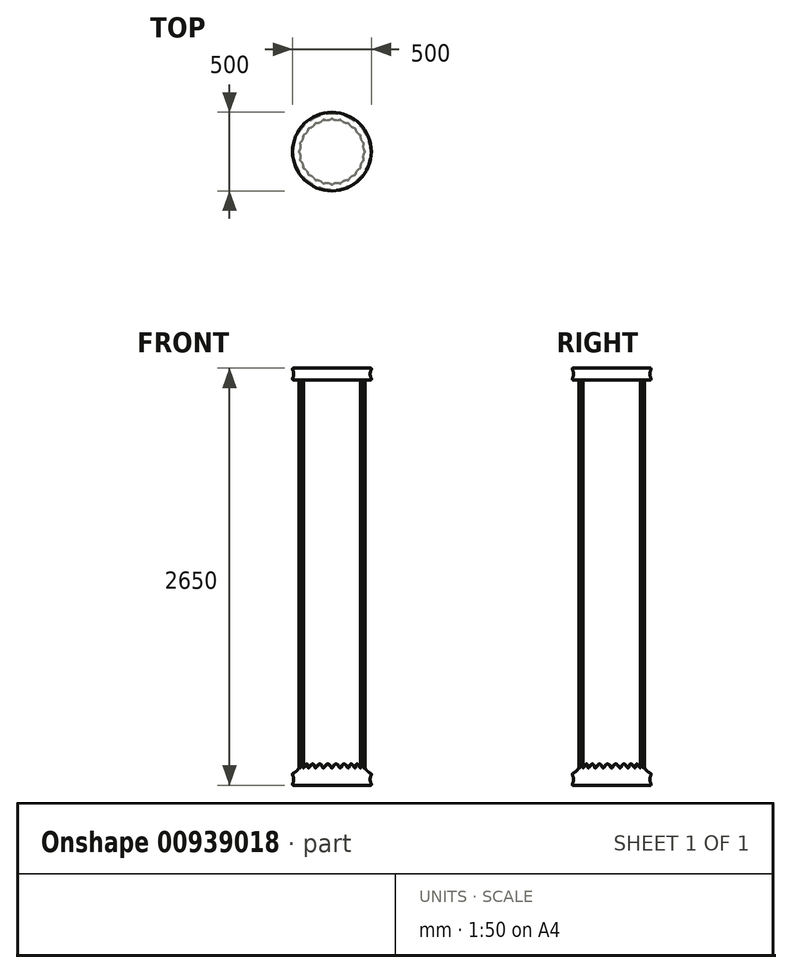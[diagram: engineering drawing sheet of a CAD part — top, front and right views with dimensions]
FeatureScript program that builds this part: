
annotation { "Feature Type Name" : "Feature", "Feature Type Description" : "" }
export const myFeature = defineFeature(function(context is Context, id is Id, definition is map)
    precondition{}
    {
        {
            var Q0;
            Q0=qCreatedBy(makeId("Front.planeOp"),FACE);
            var sketch = newSketch(context, id + "F0", { "sketchPlane" : qUnion([Q0])});
            skLineSegment(sketch, "E0", {"start": v(0, 0) * mm, "end": v(250, 0) * mm});
            skLineSegment(sketch, "E1", {"start": v(200, 147.6) * mm, "end": v(0, 147.6) * mm});
            skLineSegment(sketch, "E2", {"start": v(0, 147.6) * mm, "end": v(0, 0) * mm});
            skLineSegment(sketch, "E3", {"start": v(0, 147.6) * mm, "end": v(0, 2575) * mm});
            skLineSegment(sketch, "E4", {"start": v(0, 2575) * mm, "end": v(0, 2650) * mm});
            skLineSegment(sketch, "E5", {"start": v(0, 2650) * mm, "end": v(250, 2650) * mm});
            skLineSegment(sketch, "E6", {"start": v(250, 2575) * mm, "end": v(0, 2575) * mm});
            skLineSegment(sketch, "E7", {"start": v(250, 0) * mm, "end": v(250, 10) * mm});
            skArc(sketch, "E8", {"start": v(250, 65) * mm, "mid": v(242.63, 37.5) * mm, "end": v(250, 10) * mm});
            skLineSegment(sketch, "E9", {"start": v(250, 65) * mm, "end": v(250, 75) * mm});
            skLineSegment(sketch, "E10", {"start": v(250, 75) * mm, "end": v(200, 75) * mm});
            skLineSegment(sketch, "E11", {"start": v(200, 75) * mm, "end": v(200, 147.6) * mm});
            skLineSegment(sketch, "E12", {"start": v(250, 2650) * mm, "end": v(250, 2640) * mm});
            skLineSegment(sketch, "E13", {"start": v(250, 2575) * mm, "end": v(250, 2585) * mm});
            skArc(sketch, "E14", {"start": v(250, 2640) * mm, "mid": v(242.63, 2612.5) * mm, "end": v(250, 2585) * mm});
            skArc(sketch, "E15", {"start": v(200, 147.6) * mm, "mid": v(213.7, 103.52) * mm, "end": v(250, 75) * mm});
            skSolve(sketch);
        }
        {
            var Q0;
            Q0 = qSketchRegion(id + "F0", true);
            var Q1;
            Q1=sQuery(id+"F0.wireOp",EDGE,"E3");
            revolve(context, id + "F1", {"surfaceOperationType" : NewSurfaceOperationType.NEW, "entities" : qUnion([Q0]), "axis" : qUnion([Q1]), "revolveType" : RevolveType.FULL});
        }
        {
            var Q0;
            Q0=makeQuery(id+"F1.opRevolve","SWEPT_FACE",FACE,{"disambiguationData":[OSD([sQuery(id+"F0.wireOp",EDGE,"E1")])]});
            var sketch = newSketch(context, id + "F2", { "sketchPlane" : qUnion([Q0])});
            skCircle(sketch, "E16.cCircle", {"center": v(0, 0) * mm, "radius": 208.2 * mm, "construction": true});
            skLineSegment(sketch, "E16.0", {"start": v(202.84, 54.35) * mm, "end": v(210, 0) * mm});
            skLineSegment(sketch, "E16.1", {"start": v(210, 0) * mm, "end": v(202.84, -54.35) * mm});
            skLineSegment(sketch, "E16.2", {"start": v(202.84, -54.35) * mm, "end": v(181.87, -105) * mm});
            skLineSegment(sketch, "E16.3", {"start": v(181.87, -105) * mm, "end": v(148.5, -148.5) * mm});
            skLineSegment(sketch, "E16.4", {"start": v(148.5, -148.5) * mm, "end": v(105, -181.87) * mm});
            skLineSegment(sketch, "E16.5", {"start": v(105, -181.87) * mm, "end": v(54.35, -202.84) * mm});
            skLineSegment(sketch, "E16.6", {"start": v(54.35, -202.84) * mm, "end": v(0, -210) * mm});
            skLineSegment(sketch, "E16.7", {"start": v(0, -210) * mm, "end": v(-54.35, -202.84) * mm});
            skLineSegment(sketch, "E16.8", {"start": v(-54.35, -202.84) * mm, "end": v(-105, -181.87) * mm});
            skLineSegment(sketch, "E16.9", {"start": v(-105, -181.87) * mm, "end": v(-148.5, -148.5) * mm});
            skLineSegment(sketch, "E16.10", {"start": v(-148.5, -148.5) * mm, "end": v(-181.87, -105) * mm});
            skLineSegment(sketch, "E16.11", {"start": v(-181.87, -105) * mm, "end": v(-202.84, -54.35) * mm});
            skLineSegment(sketch, "E16.12", {"start": v(-202.84, -54.35) * mm, "end": v(-210, 0) * mm});
            skLineSegment(sketch, "E16.13", {"start": v(-210, 0) * mm, "end": v(-202.84, 54.35) * mm});
            skLineSegment(sketch, "E16.14", {"start": v(-202.84, 54.35) * mm, "end": v(-181.87, 105) * mm});
            skLineSegment(sketch, "E16.15", {"start": v(-181.87, 105) * mm, "end": v(-148.5, 148.5) * mm});
            skLineSegment(sketch, "E16.16", {"start": v(-148.5, 148.5) * mm, "end": v(-105, 181.87) * mm});
            skLineSegment(sketch, "E16.17", {"start": v(-105, 181.87) * mm, "end": v(-54.35, 202.84) * mm});
            skLineSegment(sketch, "E16.18", {"start": v(-54.35, 202.84) * mm, "end": v(0, 210) * mm});
            skLineSegment(sketch, "E16.19", {"start": v(0, 210) * mm, "end": v(54.35, 202.84) * mm});
            skLineSegment(sketch, "E16.20", {"start": v(54.35, 202.84) * mm, "end": v(105, 181.87) * mm});
            skLineSegment(sketch, "E16.21", {"start": v(105, 181.87) * mm, "end": v(148.5, 148.5) * mm});
            skLineSegment(sketch, "E16.22", {"start": v(148.5, 148.5) * mm, "end": v(181.87, 105) * mm});
            skLineSegment(sketch, "E16.23", {"start": v(181.87, 105) * mm, "end": v(202.84, 54.35) * mm});
            skLineSegment(sketch, "E17", {"start": v(0, 0) * mm, "end": v(210, 0) * mm});
            skArc(sketch, "E18", {"start": v(202.84, 54.35) * mm, "mid": v(199.17, 26.22) * mm, "end": v(210, 0) * mm});
            skArc(sketch, "E19", {"start": v(181.87, 105) * mm, "mid": v(185.6, 76.88) * mm, "end": v(202.84, 54.35) * mm});
            skArc(sketch, "E20", {"start": v(148.5, 148.5) * mm, "mid": v(159.37, 122.3) * mm, "end": v(181.87, 105) * mm});
            skArc(sketch, "E21", {"start": v(105, 181.87) * mm, "mid": v(122.3, 159.37) * mm, "end": v(148.5, 148.5) * mm});
            skArc(sketch, "E22", {"start": v(54.35, 202.84) * mm, "mid": v(76.88, 185.6) * mm, "end": v(105, 181.87) * mm});
            skArc(sketch, "E23", {"start": v(-54.35, 202.84) * mm, "mid": v(-26.22, 199.17) * mm, "end": v(0, 210) * mm});
            skArc(sketch, "E24", {"start": v(0, 210) * mm, "mid": v(26.22, 199.17) * mm, "end": v(54.35, 202.84) * mm});
            skArc(sketch, "E25", {"start": v(-105, 181.87) * mm, "mid": v(-76.88, 185.6) * mm, "end": v(-54.35, 202.84) * mm});
            skArc(sketch, "E26", {"start": v(-148.5, 148.5) * mm, "mid": v(-122.3, 159.37) * mm, "end": v(-105, 181.87) * mm});
            skArc(sketch, "E27", {"start": v(-181.87, 105) * mm, "mid": v(-159.37, 122.3) * mm, "end": v(-148.5, 148.5) * mm});
            skArc(sketch, "E28", {"start": v(-202.84, 54.35) * mm, "mid": v(-185.6, 76.88) * mm, "end": v(-181.87, 105) * mm});
            skArc(sketch, "E29", {"start": v(-210, 0) * mm, "mid": v(-199.17, 26.22) * mm, "end": v(-202.84, 54.35) * mm});
            skArc(sketch, "E30", {"start": v(-202.84, -54.35) * mm, "mid": v(-199.17, -26.22) * mm, "end": v(-210, 0) * mm});
            skArc(sketch, "E31", {"start": v(-181.87, -105) * mm, "mid": v(-185.6, -76.88) * mm, "end": v(-202.84, -54.35) * mm});
            skArc(sketch, "E32", {"start": v(-148.5, -148.5) * mm, "mid": v(-159.37, -122.3) * mm, "end": v(-181.87, -105) * mm});
            skArc(sketch, "E33", {"start": v(-105, -181.87) * mm, "mid": v(-122.3, -159.37) * mm, "end": v(-148.5, -148.5) * mm});
            skArc(sketch, "E34", {"start": v(-54.35, -202.84) * mm, "mid": v(-76.88, -185.6) * mm, "end": v(-105, -181.87) * mm});
            skArc(sketch, "E35", {"start": v(0, -210) * mm, "mid": v(-26.22, -199.17) * mm, "end": v(-54.35, -202.84) * mm});
            skArc(sketch, "E36", {"start": v(54.35, -202.84) * mm, "mid": v(26.22, -199.17) * mm, "end": v(0, -210) * mm});
            skArc(sketch, "E37", {"start": v(105, -181.87) * mm, "mid": v(76.88, -185.6) * mm, "end": v(54.35, -202.84) * mm});
            skArc(sketch, "E38", {"start": v(148.5, -148.5) * mm, "mid": v(122.3, -159.37) * mm, "end": v(105, -181.87) * mm});
            skArc(sketch, "E39", {"start": v(181.87, -105) * mm, "mid": v(159.37, -122.3) * mm, "end": v(148.5, -148.5) * mm});
            skArc(sketch, "E40", {"start": v(202.84, -54.35) * mm, "mid": v(185.6, -76.88) * mm, "end": v(181.87, -105) * mm});
            skArc(sketch, "E41", {"start": v(210, 0) * mm, "mid": v(199.17, -26.22) * mm, "end": v(202.84, -54.35) * mm});
            skSolve(sketch);
        }
        {
            var Q0;
            Q0=makeQuery(id+"F2.imprint","IMPRINT",FACE,{"disambiguationData":[TD([[makeQuery(id+"F2.imprint","IMPRINT",EDGE,{"derivedFrom":makeQuery(id+"F1.opRevolve","SWEPT_EDGE",EDGE,{"disambiguationData":[OSD([sQuery(id+"F0.wireOp",EDGE,"E1"),sQuery(id+"F0.wireOp",EDGE,"E11"),sQuery(id+"F0.wireOp",EDGE,"A7NMMrHn-6jUg-eE0d-P7Q7-RPc74vaHHU1M")])]})}),-1.0]])]});
            var Q1;
            Q1=makeQuery(id+"F2.imprint","IMPRINT",FACE,{"disambiguationData":[TD([[makeQuery(id+"F2.imprint","IMPRINT",EDGE,{"derivedFrom":sQuery(id+"F2.wireOp",EDGE,"E18")}),-1.0]])]});
            extrude(context, id + "F3", {"entities" : qUnion([Q0, Q1]), "operationType" : NewBodyOperationType.ADD, "depth" : 2500 * mm, "offsetDistance" : 25 * mm, "hasSecondDirection" : true, "secondDirectionOppositeDirection" : true, "secondDirectionDepth" : 50 * mm});
        }
        {
            var Q0;
            Q0=makeQuery(id+"F3.opExtrude","SWEPT_FACE",FACE,{"disambiguationData":[OSD([sQuery(id+"F2.wireOp",EDGE,"E35")])]});
            var Q1;
            Q1=makeQuery(id+"F1.opRevolve","SWEPT_FACE",FACE,{"disambiguationData":[OSD([sQuery(id+"F0.wireOp",EDGE,"E7")])]});
            var Q2;
            Q2=makeQuery(id+"F3.opExtrude","SWEPT_FACE",FACE,{"disambiguationData":[OSD([sQuery(id+"F2.wireOp",EDGE,"E36")])]});
            var Q3;
            Q3=makeQuery(id+"F3.opExtrude","SWEPT_FACE",FACE,{"disambiguationData":[OSD([sQuery(id+"F2.wireOp",EDGE,"E32")])]});
            var Q4;
            Q4=makeQuery(id+"F1.opRevolve","SWEPT_EDGE",EDGE,{"disambiguationData":[OSD([sQuery(id+"F0.wireOp",EDGE,"E0"),sQuery(id+"F0.wireOp",EDGE,"E7")])]});
            var Q5;
            Q5=makeQuery(id+"F1.opRevolve","SWEPT_EDGE",EDGE,{"disambiguationData":[OSD([sQuery(id+"F0.wireOp",EDGE,"E13"),sQuery(id+"F0.wireOp",EDGE,"E14")])]});
            var Q6;
            Q6=makeQuery(id+"F1.opRevolve","SWEPT_FACE",FACE,{"disambiguationData":[OSD([sQuery(id+"F0.wireOp",EDGE,"E13")])]});
            var Q7;
            Q7=makeQuery(id+"F1.opRevolve","SWEPT_FACE",FACE,{"disambiguationData":[OSD([sQuery(id+"F0.wireOp",EDGE,"E0")])]});
            var Q8;
            Q8=makeQuery(id+"F1.opRevolve","SWEPT_FACE",FACE,{"disambiguationData":[OSD([sQuery(id+"F0.wireOp",EDGE,"E12")])]});
            var Q9;
            Q9=makeQuery(id+"F1.opRevolve","SWEPT_FACE",FACE,{"disambiguationData":[OSD([sQuery(id+"F0.wireOp",EDGE,"E9")])]});
            var Q10;
            Q10=makeQuery(id+"F3.opExtrude","SWEPT_FACE",FACE,{"disambiguationData":[OSD([sQuery(id+"F2.wireOp",EDGE,"E38")])]});
            var Q11;
            Q11=makeQuery(id+"F1.opRevolve","SWEPT_FACE",FACE,{"disambiguationData":[OSD([sQuery(id+"F0.wireOp",EDGE,"E14")])]});
            var Q12;
            Q12=makeQuery(id+"F1.opRevolve","SWEPT_FACE",FACE,{"disambiguationData":[OSD([sQuery(id+"F0.wireOp",EDGE,"E6")])]});
            var Q13;
            Q13=makeQuery(id+"F3.opExtrude","SWEPT_FACE",FACE,{"disambiguationData":[OSD([sQuery(id+"F2.wireOp",EDGE,"E40")])]});
            var Q14;
            Q14=makeQuery(id+"F3.opExtrude","SWEPT_FACE",FACE,{"disambiguationData":[OSD([sQuery(id+"F2.wireOp",EDGE,"E33")])]});
            var Q15;
            Q15=makeQuery(id+"F1.opRevolve","SWEPT_FACE",FACE,{"disambiguationData":[OSD([sQuery(id+"F0.wireOp",EDGE,"E8")])]});
            var Q16;
            Q16=makeQuery(id+"F1.opRevolve","SWEPT_FACE",FACE,{"disambiguationData":[OSD([sQuery(id+"F0.wireOp",EDGE,"E15")])]});
            var Q17;
            Q17=makeQuery(id+"F3.opExtrude","SWEPT_FACE",FACE,{"disambiguationData":[OSD([sQuery(id+"F2.wireOp",EDGE,"E34")])]});
            var Q18;
            Q18=makeQuery(id+"F3.opExtrude","SWEPT_FACE",FACE,{"disambiguationData":[OSD([sQuery(id+"F2.wireOp",EDGE,"E37")])]});
            var Q19;
            Q19=makeQuery(id+"F1.opRevolve","SWEPT_EDGE",EDGE,{"disambiguationData":[OSD([sQuery(id+"F0.wireOp",EDGE,"E6"),sQuery(id+"F0.wireOp",EDGE,"E13")])]});
            var Q20;
            Q20=makeQuery(id+"F1.opRevolve","SWEPT_FACE",FACE,{"disambiguationData":[OSD([sQuery(id+"F0.wireOp",EDGE,"E5")])]});
            var Q21;
            Q21=makeQuery(id+"F3.opExtrude","SWEPT_FACE",FACE,{"disambiguationData":[OSD([sQuery(id+"F2.wireOp",EDGE,"E39")])]});
            var Q22;
            Q22=makeQuery(id+"F3.opExtrude","SWEPT_FACE",FACE,{"disambiguationData":[OSD([sQuery(id+"F2.wireOp",EDGE,"E31")])]});
            var Q23;
            Q23=makeQuery(id+"F3.boolean.opBoolean","INTERSECT",EDGE,{"derivedFrom":[makeQuery(id+"F1.opRevolve","SWEPT_FACE",FACE,{"disambiguationData":[OSD([sQuery(id+"F0.wireOp",EDGE,"E15")])]}),makeQuery(id+"F3.opExtrude","SWEPT_FACE",FACE,{"disambiguationData":[OSD([sQuery(id+"F2.wireOp",EDGE,"E39")])]})]});
            var Q24;
            Q24=makeQuery(id+"F3.opExtrude","SWEPT_FACE",FACE,{"disambiguationData":[OSD([sQuery(id+"F2.wireOp",EDGE,"E23")])]});
            var Q25;
            Q25=makeQuery(id+"F3.boolean.opBoolean","INTERSECT",EDGE,{"derivedFrom":[makeQuery(id+"F1.opRevolve","SWEPT_FACE",FACE,{"disambiguationData":[OSD([sQuery(id+"F0.wireOp",EDGE,"E15")])]}),makeQuery(id+"F3.opExtrude","SWEPT_FACE",FACE,{"disambiguationData":[OSD([sQuery(id+"F2.wireOp",EDGE,"E38")])]})]});
            var Q26;
            Q26=makeQuery(id+"F3.opExtrude","SWEPT_FACE",FACE,{"disambiguationData":[OSD([sQuery(id+"F2.wireOp",EDGE,"E20")])]});
            var Q27;
            Q27=makeQuery(id+"F3.boolean.opBoolean","INTERSECT",EDGE,{"derivedFrom":[makeQuery(id+"F1.opRevolve","SWEPT_FACE",FACE,{"disambiguationData":[OSD([sQuery(id+"F0.wireOp",EDGE,"E6")])]}),makeQuery(id+"F3.opExtrude","SWEPT_FACE",FACE,{"disambiguationData":[OSD([sQuery(id+"F2.wireOp",EDGE,"E38")])]})]});
            var Q28;
            Q28=makeQuery(id+"F3.opExtrude","SWEPT_EDGE",EDGE,{"disambiguationData":[OSD([sQuery(id+"F2.wireOp",EDGE,"E16.9"),sQuery(id+"F2.wireOp",EDGE,"E16.10"),sQuery(id+"F2.wireOp",EDGE,"E32"),sQuery(id+"F2.wireOp",EDGE,"E33")])]});
            var Q29;
            Q29=makeQuery(id+"F3.boolean.opBoolean","INTERSECT",EDGE,{"derivedFrom":[makeQuery(id+"F1.opRevolve","SWEPT_FACE",FACE,{"disambiguationData":[OSD([sQuery(id+"F0.wireOp",EDGE,"E6")])]}),makeQuery(id+"F3.opExtrude","SWEPT_FACE",FACE,{"disambiguationData":[OSD([sQuery(id+"F2.wireOp",EDGE,"E39")])]})]});
            var Q30;
            Q30=makeQuery(id+"F3.boolean.opBoolean","INTERSECT",EDGE,{"derivedFrom":[makeQuery(id+"F1.opRevolve","SWEPT_FACE",FACE,{"disambiguationData":[OSD([sQuery(id+"F0.wireOp",EDGE,"E6")])]}),makeQuery(id+"F3.opExtrude","SWEPT_FACE",FACE,{"disambiguationData":[OSD([sQuery(id+"F2.wireOp",EDGE,"E35")])]})]});
            var Q31;
            Q31=makeQuery(id+"F3.opExtrude","SWEPT_EDGE",EDGE,{"disambiguationData":[OSD([sQuery(id+"F2.wireOp",EDGE,"E16.3"),sQuery(id+"F2.wireOp",EDGE,"E16.4"),sQuery(id+"F2.wireOp",EDGE,"E38"),sQuery(id+"F2.wireOp",EDGE,"E39")])]});
            var Q32;
            Q32=makeQuery(id+"F3.boolean.opBoolean","INTERSECT",EDGE,{"derivedFrom":[makeQuery(id+"F1.opRevolve","SWEPT_FACE",FACE,{"disambiguationData":[OSD([sQuery(id+"F0.wireOp",EDGE,"E15")])]}),makeQuery(id+"F3.opExtrude","SWEPT_FACE",FACE,{"disambiguationData":[OSD([sQuery(id+"F2.wireOp",EDGE,"E35")])]})]});
            var Q33;
            Q33=makeQuery(id+"F3.boolean.opBoolean","INTERSECT",EDGE,{"derivedFrom":[makeQuery(id+"F1.opRevolve","SWEPT_FACE",FACE,{"disambiguationData":[OSD([sQuery(id+"F0.wireOp",EDGE,"E6")])]}),makeQuery(id+"F3.opExtrude","SWEPT_FACE",FACE,{"disambiguationData":[OSD([sQuery(id+"F2.wireOp",EDGE,"E36")])]})]});
            var Q34;
            Q34=makeQuery(id+"F3.boolean.opBoolean","INTERSECT",EDGE,{"derivedFrom":[makeQuery(id+"F1.opRevolve","SWEPT_FACE",FACE,{"disambiguationData":[OSD([sQuery(id+"F0.wireOp",EDGE,"E15")])]}),makeQuery(id+"F3.opExtrude","SWEPT_FACE",FACE,{"disambiguationData":[OSD([sQuery(id+"F2.wireOp",EDGE,"E31")])]})]});
            var Q35;
            Q35=makeQuery(id+"F3.opExtrude","SWEPT_FACE",FACE,{"disambiguationData":[OSD([sQuery(id+"F2.wireOp",EDGE,"E21")])]});
            var Q36;
            Q36=makeQuery(id+"F3.boolean.opBoolean","INTERSECT",EDGE,{"derivedFrom":[makeQuery(id+"F1.opRevolve","SWEPT_FACE",FACE,{"disambiguationData":[OSD([sQuery(id+"F0.wireOp",EDGE,"E15")])]}),makeQuery(id+"F3.opExtrude","SWEPT_FACE",FACE,{"disambiguationData":[OSD([sQuery(id+"F2.wireOp",EDGE,"E37")])]})]});
            var Q37;
            Q37=makeQuery(id+"F3.boolean.opBoolean","INTERSECT",EDGE,{"derivedFrom":[makeQuery(id+"F1.opRevolve","SWEPT_FACE",FACE,{"disambiguationData":[OSD([sQuery(id+"F0.wireOp",EDGE,"E15")])]}),makeQuery(id+"F3.opExtrude","SWEPT_FACE",FACE,{"disambiguationData":[OSD([sQuery(id+"F2.wireOp",EDGE,"E34")])]})]});
            var Q38;
            Q38=makeQuery(id+"F3.opExtrude","SWEPT_FACE",FACE,{"disambiguationData":[OSD([sQuery(id+"F2.wireOp",EDGE,"E22")])]});
            var Q39;
            Q39=makeQuery(id+"F3.opExtrude","SWEPT_EDGE",EDGE,{"disambiguationData":[OSD([sQuery(id+"F2.wireOp",EDGE,"E16.2"),sQuery(id+"F2.wireOp",EDGE,"E16.3"),sQuery(id+"F2.wireOp",EDGE,"E39"),sQuery(id+"F2.wireOp",EDGE,"E40")])]});
            var Q40;
            Q40=makeQuery(id+"F3.opExtrude","SWEPT_EDGE",EDGE,{"disambiguationData":[OSD([sQuery(id+"F2.wireOp",EDGE,"E16.6"),sQuery(id+"F2.wireOp",EDGE,"E16.7"),sQuery(id+"F2.wireOp",EDGE,"E35"),sQuery(id+"F2.wireOp",EDGE,"E36")])]});
            var Q41;
            Q41=makeQuery(id+"F3.opExtrude","SWEPT_EDGE",EDGE,{"disambiguationData":[OSD([sQuery(id+"F2.wireOp",EDGE,"E16.10"),sQuery(id+"F2.wireOp",EDGE,"E16.11"),sQuery(id+"F2.wireOp",EDGE,"E31"),sQuery(id+"F2.wireOp",EDGE,"E32")])]});
            var Q42;
            Q42=makeQuery(id+"F3.opExtrude","SWEPT_FACE",FACE,{"disambiguationData":[OSD([sQuery(id+"F2.wireOp",EDGE,"E27")])]});
            var Q43;
            Q43=makeQuery(id+"F3.opExtrude","SWEPT_FACE",FACE,{"disambiguationData":[OSD([sQuery(id+"F2.wireOp",EDGE,"E26")])]});
            var Q44;
            Q44=makeQuery(id+"F3.boolean.opBoolean","INTERSECT",EDGE,{"derivedFrom":[makeQuery(id+"F1.opRevolve","SWEPT_FACE",FACE,{"disambiguationData":[OSD([sQuery(id+"F0.wireOp",EDGE,"E6")])]}),makeQuery(id+"F3.opExtrude","SWEPT_FACE",FACE,{"disambiguationData":[OSD([sQuery(id+"F2.wireOp",EDGE,"E34")])]})]});
            var Q45;
            Q45=makeQuery(id+"F1.opRevolve","SWEPT_EDGE",EDGE,{"disambiguationData":[OSD([sQuery(id+"F0.wireOp",EDGE,"E7"),sQuery(id+"F0.wireOp",EDGE,"E8")])]});
            var Q46;
            Q46=makeQuery(id+"F3.boolean.opBoolean","INTERSECT",EDGE,{"derivedFrom":[makeQuery(id+"F1.opRevolve","SWEPT_FACE",FACE,{"disambiguationData":[OSD([sQuery(id+"F0.wireOp",EDGE,"E15")])]}),makeQuery(id+"F3.opExtrude","SWEPT_FACE",FACE,{"disambiguationData":[OSD([sQuery(id+"F2.wireOp",EDGE,"E32")])]})]});
            var Q47;
            Q47=makeQuery(id+"F3.opExtrude","SWEPT_EDGE",EDGE,{"disambiguationData":[OSD([sQuery(id+"F2.wireOp",EDGE,"E16.5"),sQuery(id+"F2.wireOp",EDGE,"E16.6"),sQuery(id+"F2.wireOp",EDGE,"E36"),sQuery(id+"F2.wireOp",EDGE,"E37")])]});
            var Q48;
            Q48=makeQuery(id+"F3.opExtrude","SWEPT_FACE",FACE,{"disambiguationData":[OSD([sQuery(id+"F2.wireOp",EDGE,"E41")])]});
            var Q49;
            Q49=makeQuery(id+"F3.boolean.opBoolean","INTERSECT",EDGE,{"derivedFrom":[makeQuery(id+"F1.opRevolve","SWEPT_FACE",FACE,{"disambiguationData":[OSD([sQuery(id+"F0.wireOp",EDGE,"E6")])]}),makeQuery(id+"F3.opExtrude","SWEPT_FACE",FACE,{"disambiguationData":[OSD([sQuery(id+"F2.wireOp",EDGE,"E37")])]})]});
            var Q50;
            Q50=makeQuery(id+"F3.opExtrude","SWEPT_FACE",FACE,{"disambiguationData":[OSD([sQuery(id+"F2.wireOp",EDGE,"E25")])]});
            var Q51;
            Q51=makeQuery(id+"F3.boolean.opBoolean","INTERSECT",EDGE,{"derivedFrom":[makeQuery(id+"F1.opRevolve","SWEPT_FACE",FACE,{"disambiguationData":[OSD([sQuery(id+"F0.wireOp",EDGE,"E15")])]}),makeQuery(id+"F3.opExtrude","SWEPT_FACE",FACE,{"disambiguationData":[OSD([sQuery(id+"F2.wireOp",EDGE,"E33")])]})]});
            var Q52;
            Q52=makeQuery(id+"F3.opExtrude","SWEPT_EDGE",EDGE,{"disambiguationData":[OSD([sQuery(id+"F2.wireOp",EDGE,"E16.8"),sQuery(id+"F2.wireOp",EDGE,"E16.9"),sQuery(id+"F2.wireOp",EDGE,"E33"),sQuery(id+"F2.wireOp",EDGE,"E34")])]});
            var Q53;
            Q53=makeQuery(id+"F3.boolean.opBoolean","INTERSECT",EDGE,{"derivedFrom":[makeQuery(id+"F1.opRevolve","SWEPT_FACE",FACE,{"disambiguationData":[OSD([sQuery(id+"F0.wireOp",EDGE,"E15")])]}),makeQuery(id+"F3.opExtrude","SWEPT_FACE",FACE,{"disambiguationData":[OSD([sQuery(id+"F2.wireOp",EDGE,"E36")])]})]});
            var Q54;
            Q54=makeQuery(id+"F3.opExtrude","SWEPT_FACE",FACE,{"disambiguationData":[OSD([sQuery(id+"F2.wireOp",EDGE,"E30")])]});
            var Q55;
            Q55=makeQuery(id+"F3.opExtrude","SWEPT_EDGE",EDGE,{"disambiguationData":[OSD([sQuery(id+"F2.wireOp",EDGE,"E16.7"),sQuery(id+"F2.wireOp",EDGE,"E16.8"),sQuery(id+"F2.wireOp",EDGE,"E34"),sQuery(id+"F2.wireOp",EDGE,"E35")])]});
            var Q56;
            Q56=makeQuery(id+"F1.opRevolve","SWEPT_EDGE",EDGE,{"disambiguationData":[OSD([sQuery(id+"F0.wireOp",EDGE,"E12"),sQuery(id+"F0.wireOp",EDGE,"E14")])]});
            var Q57;
            Q57=makeQuery(id+"F3.opExtrude","SWEPT_EDGE",EDGE,{"disambiguationData":[OSD([sQuery(id+"F2.wireOp",EDGE,"E16.4"),sQuery(id+"F2.wireOp",EDGE,"E16.5"),sQuery(id+"F2.wireOp",EDGE,"E37"),sQuery(id+"F2.wireOp",EDGE,"E38")])]});
            var Q58;
            Q58=makeQuery(id+"F3.boolean.opBoolean","INTERSECT",EDGE,{"derivedFrom":[makeQuery(id+"F1.opRevolve","SWEPT_FACE",FACE,{"disambiguationData":[OSD([sQuery(id+"F0.wireOp",EDGE,"E6")])]}),makeQuery(id+"F3.opExtrude","SWEPT_FACE",FACE,{"disambiguationData":[OSD([sQuery(id+"F2.wireOp",EDGE,"E33")])]})]});
            var Q59;
            Q59=makeQuery(id+"F3.boolean.opBoolean","INTERSECT",EDGE,{"derivedFrom":[makeQuery(id+"F1.opRevolve","SWEPT_FACE",FACE,{"disambiguationData":[OSD([sQuery(id+"F0.wireOp",EDGE,"E6")])]}),makeQuery(id+"F3.opExtrude","SWEPT_FACE",FACE,{"disambiguationData":[OSD([sQuery(id+"F2.wireOp",EDGE,"E32")])]})]});
            var Q60;
            Q60=makeQuery(id+"F3.boolean.opBoolean","INTERSECT",EDGE,{"derivedFrom":[makeQuery(id+"F1.opRevolve","SWEPT_FACE",FACE,{"disambiguationData":[OSD([sQuery(id+"F0.wireOp",EDGE,"E6")])]}),makeQuery(id+"F3.opExtrude","SWEPT_FACE",FACE,{"disambiguationData":[OSD([sQuery(id+"F2.wireOp",EDGE,"E31")])]})]});
            var Q61;
            Q61=makeQuery(id+"F3.boolean.opBoolean","INTERSECT",EDGE,{"derivedFrom":[makeQuery(id+"F1.opRevolve","SWEPT_FACE",FACE,{"disambiguationData":[OSD([sQuery(id+"F0.wireOp",EDGE,"E6")])]}),makeQuery(id+"F3.opExtrude","SWEPT_FACE",FACE,{"disambiguationData":[OSD([sQuery(id+"F2.wireOp",EDGE,"E40")])]})]});
            var Q62;
            Q62=makeQuery(id+"F1.opRevolve","SWEPT_EDGE",EDGE,{"disambiguationData":[OSD([sQuery(id+"F0.wireOp",EDGE,"E9"),sQuery(id+"F0.wireOp",EDGE,"E10"),sQuery(id+"F0.wireOp",EDGE,"E15")])]});
            var Q63;
            Q63=makeQuery(id+"F3.boolean.opBoolean","INTERSECT",EDGE,{"derivedFrom":[makeQuery(id+"F1.opRevolve","SWEPT_FACE",FACE,{"disambiguationData":[OSD([sQuery(id+"F0.wireOp",EDGE,"E15")])]}),makeQuery(id+"F3.opExtrude","SWEPT_FACE",FACE,{"disambiguationData":[OSD([sQuery(id+"F2.wireOp",EDGE,"E40")])]})]});
            var Q64;
            Q64=makeQuery(id+"F3.opExtrude","SWEPT_FACE",FACE,{"disambiguationData":[OSD([sQuery(id+"F2.wireOp",EDGE,"E24")])]});
            var Q65;
            Q65=makeQuery(id+"F3.opExtrude","SWEPT_EDGE",EDGE,{"disambiguationData":[OSD([sQuery(id+"F2.wireOp",EDGE,"E16.1"),sQuery(id+"F2.wireOp",EDGE,"E16.2"),sQuery(id+"F2.wireOp",EDGE,"E40"),sQuery(id+"F2.wireOp",EDGE,"E41")])]});
            var Q66;
            Q66=makeQuery(id+"F3.boolean.opBoolean","INTERSECT",EDGE,{"derivedFrom":[makeQuery(id+"F1.opRevolve","SWEPT_FACE",FACE,{"disambiguationData":[OSD([sQuery(id+"F0.wireOp",EDGE,"E15")])]}),makeQuery(id+"F3.opExtrude","SWEPT_FACE",FACE,{"disambiguationData":[OSD([sQuery(id+"F2.wireOp",EDGE,"E30")])]})]});
            var Q67;
            Q67=makeQuery(id+"F3.opExtrude","SWEPT_EDGE",EDGE,{"disambiguationData":[OSD([sQuery(id+"F2.wireOp",EDGE,"E16.21"),sQuery(id+"F2.wireOp",EDGE,"E16.22"),sQuery(id+"F2.wireOp",EDGE,"E20"),sQuery(id+"F2.wireOp",EDGE,"E21")])]});
            var Q68;
            Q68=makeQuery(id+"F3.boolean.opBoolean","INTERSECT",EDGE,{"derivedFrom":[makeQuery(id+"F1.opRevolve","SWEPT_FACE",FACE,{"disambiguationData":[OSD([sQuery(id+"F0.wireOp",EDGE,"E6")])]}),makeQuery(id+"F3.opExtrude","SWEPT_FACE",FACE,{"disambiguationData":[OSD([sQuery(id+"F2.wireOp",EDGE,"E27")])]})]});
            var Q69;
            Q69=makeQuery(id+"F3.opExtrude","SWEPT_FACE",FACE,{"disambiguationData":[OSD([sQuery(id+"F2.wireOp",EDGE,"E28")])]});
            var Q70;
            Q70=makeQuery(id+"F3.opExtrude","SWEPT_FACE",FACE,{"disambiguationData":[OSD([sQuery(id+"F2.wireOp",EDGE,"E18")])]});
            var Q71;
            Q71=makeQuery(id+"F3.boolean.opBoolean","INTERSECT",EDGE,{"derivedFrom":[makeQuery(id+"F1.opRevolve","SWEPT_FACE",FACE,{"disambiguationData":[OSD([sQuery(id+"F0.wireOp",EDGE,"E15")])]}),makeQuery(id+"F3.opExtrude","SWEPT_FACE",FACE,{"disambiguationData":[OSD([sQuery(id+"F2.wireOp",EDGE,"E25")])]})]});
            var Q72;
            Q72=makeQuery(id+"F3.boolean.opBoolean","INTERSECT",EDGE,{"derivedFrom":[makeQuery(id+"F1.opRevolve","SWEPT_FACE",FACE,{"disambiguationData":[OSD([sQuery(id+"F0.wireOp",EDGE,"E15")])]}),makeQuery(id+"F3.opExtrude","SWEPT_FACE",FACE,{"disambiguationData":[OSD([sQuery(id+"F2.wireOp",EDGE,"E20")])]})]});
            var Q73;
            Q73=makeQuery(id+"F3.boolean.opBoolean","INTERSECT",EDGE,{"derivedFrom":[makeQuery(id+"F1.opRevolve","SWEPT_FACE",FACE,{"disambiguationData":[OSD([sQuery(id+"F0.wireOp",EDGE,"E6")])]}),makeQuery(id+"F3.opExtrude","SWEPT_FACE",FACE,{"disambiguationData":[OSD([sQuery(id+"F2.wireOp",EDGE,"E20")])]})]});
            var Q74;
            Q74=makeQuery(id+"F3.opExtrude","SWEPT_FACE",FACE,{"disambiguationData":[OSD([sQuery(id+"F2.wireOp",EDGE,"E19")])]});
            var Q75;
            Q75=makeQuery(id+"F3.boolean.opBoolean","INTERSECT",EDGE,{"derivedFrom":[makeQuery(id+"F1.opRevolve","SWEPT_FACE",FACE,{"disambiguationData":[OSD([sQuery(id+"F0.wireOp",EDGE,"E15")])]}),makeQuery(id+"F3.opExtrude","SWEPT_FACE",FACE,{"disambiguationData":[OSD([sQuery(id+"F2.wireOp",EDGE,"E28")])]})]});
            var Q76;
            Q76=makeQuery(id+"F3.boolean.opBoolean","INTERSECT",EDGE,{"derivedFrom":[makeQuery(id+"F1.opRevolve","SWEPT_FACE",FACE,{"disambiguationData":[OSD([sQuery(id+"F0.wireOp",EDGE,"E15")])]}),makeQuery(id+"F3.opExtrude","SWEPT_FACE",FACE,{"disambiguationData":[OSD([sQuery(id+"F2.wireOp",EDGE,"E22")])]})]});
            var Q77;
            Q77=makeQuery(id+"F3.opExtrude","SWEPT_EDGE",EDGE,{"disambiguationData":[OSD([sQuery(id+"F2.wireOp",EDGE,"E16.15"),sQuery(id+"F2.wireOp",EDGE,"E16.16"),sQuery(id+"F2.wireOp",EDGE,"E26"),sQuery(id+"F2.wireOp",EDGE,"E27")])]});
            var Q78;
            Q78=makeQuery(id+"F3.opExtrude","SWEPT_FACE",FACE,{"disambiguationData":[OSD([sQuery(id+"F2.wireOp",EDGE,"E29")])]});
            var Q79;
            Q79=makeQuery(id+"F3.opExtrude","SWEPT_EDGE",EDGE,{"disambiguationData":[OSD([sQuery(id+"F2.wireOp",EDGE,"E16.11"),sQuery(id+"F2.wireOp",EDGE,"E16.12"),sQuery(id+"F2.wireOp",EDGE,"E30"),sQuery(id+"F2.wireOp",EDGE,"E31")])]});
            var Q80;
            Q80=makeQuery(id+"F1.opRevolve","SWEPT_EDGE",EDGE,{"disambiguationData":[OSD([sQuery(id+"F0.wireOp",EDGE,"E5"),sQuery(id+"F0.wireOp",EDGE,"E12")])]});
            var Q81;
            Q81=makeQuery(id+"F3.boolean.opBoolean","INTERSECT",EDGE,{"derivedFrom":[makeQuery(id+"F1.opRevolve","SWEPT_FACE",FACE,{"disambiguationData":[OSD([sQuery(id+"F0.wireOp",EDGE,"E15")])]}),makeQuery(id+"F3.opExtrude","SWEPT_FACE",FACE,{"disambiguationData":[OSD([sQuery(id+"F2.wireOp",EDGE,"E19")])]})]});
            var Q82;
            Q82=makeQuery(id+"F3.boolean.opBoolean","INTERSECT",EDGE,{"derivedFrom":[makeQuery(id+"F1.opRevolve","SWEPT_FACE",FACE,{"disambiguationData":[OSD([sQuery(id+"F0.wireOp",EDGE,"E6")])]}),makeQuery(id+"F3.opExtrude","SWEPT_FACE",FACE,{"disambiguationData":[OSD([sQuery(id+"F2.wireOp",EDGE,"E22")])]})]});
            var Q83;
            Q83=makeQuery(id+"F3.boolean.opBoolean","INTERSECT",EDGE,{"derivedFrom":[makeQuery(id+"F1.opRevolve","SWEPT_FACE",FACE,{"disambiguationData":[OSD([sQuery(id+"F0.wireOp",EDGE,"E15")])]}),makeQuery(id+"F3.opExtrude","SWEPT_FACE",FACE,{"disambiguationData":[OSD([sQuery(id+"F2.wireOp",EDGE,"E21")])]})]});
            var Q84;
            Q84=makeQuery(id+"F3.boolean.opBoolean","INTERSECT",EDGE,{"derivedFrom":[makeQuery(id+"F1.opRevolve","SWEPT_FACE",FACE,{"disambiguationData":[OSD([sQuery(id+"F0.wireOp",EDGE,"E6")])]}),makeQuery(id+"F3.opExtrude","SWEPT_FACE",FACE,{"disambiguationData":[OSD([sQuery(id+"F2.wireOp",EDGE,"E30")])]})]});
            var Q85;
            Q85=makeQuery(id+"F3.boolean.opBoolean","INTERSECT",EDGE,{"derivedFrom":[makeQuery(id+"F1.opRevolve","SWEPT_FACE",FACE,{"disambiguationData":[OSD([sQuery(id+"F0.wireOp",EDGE,"E6")])]}),makeQuery(id+"F3.opExtrude","SWEPT_FACE",FACE,{"disambiguationData":[OSD([sQuery(id+"F2.wireOp",EDGE,"E23")])]})]});
            var Q86;
            Q86=makeQuery(id+"F3.boolean.opBoolean","INTERSECT",EDGE,{"derivedFrom":[makeQuery(id+"F1.opRevolve","SWEPT_FACE",FACE,{"disambiguationData":[OSD([sQuery(id+"F0.wireOp",EDGE,"E6")])]}),makeQuery(id+"F3.opExtrude","SWEPT_FACE",FACE,{"disambiguationData":[OSD([sQuery(id+"F2.wireOp",EDGE,"E24")])]})]});
            var Q87;
            Q87=makeQuery(id+"F3.boolean.opBoolean","INTERSECT",EDGE,{"derivedFrom":[makeQuery(id+"F1.opRevolve","SWEPT_FACE",FACE,{"disambiguationData":[OSD([sQuery(id+"F0.wireOp",EDGE,"E6")])]}),makeQuery(id+"F3.opExtrude","SWEPT_FACE",FACE,{"disambiguationData":[OSD([sQuery(id+"F2.wireOp",EDGE,"E21")])]})]});
            var Q88;
            Q88=makeQuery(id+"F3.opExtrude","SWEPT_EDGE",EDGE,{"disambiguationData":[OSD([sQuery(id+"F2.wireOp",EDGE,"E16.17"),sQuery(id+"F2.wireOp",EDGE,"E16.18"),sQuery(id+"F2.wireOp",EDGE,"E23"),sQuery(id+"F2.wireOp",EDGE,"E25")])]});
            var Q89;
            Q89=makeQuery(id+"F3.boolean.opBoolean","INTERSECT",EDGE,{"derivedFrom":[makeQuery(id+"F1.opRevolve","SWEPT_FACE",FACE,{"disambiguationData":[OSD([sQuery(id+"F0.wireOp",EDGE,"E15")])]}),makeQuery(id+"F3.opExtrude","SWEPT_FACE",FACE,{"disambiguationData":[OSD([sQuery(id+"F2.wireOp",EDGE,"E26")])]})]});
            var Q90;
            Q90=makeQuery(id+"F3.opExtrude","SWEPT_EDGE",EDGE,{"disambiguationData":[OSD([sQuery(id+"F2.wireOp",EDGE,"E16.20"),sQuery(id+"F2.wireOp",EDGE,"E16.21"),sQuery(id+"F2.wireOp",EDGE,"E21"),sQuery(id+"F2.wireOp",EDGE,"E22")])]});
            var Q91;
            Q91=makeQuery(id+"F3.opExtrude","SWEPT_EDGE",EDGE,{"disambiguationData":[OSD([sQuery(id+"F2.wireOp",EDGE,"E16.16"),sQuery(id+"F2.wireOp",EDGE,"E16.17"),sQuery(id+"F2.wireOp",EDGE,"E25"),sQuery(id+"F2.wireOp",EDGE,"E26")])]});
            var Q92;
            Q92=makeQuery(id+"F3.boolean.opBoolean","INTERSECT",EDGE,{"derivedFrom":[makeQuery(id+"F1.opRevolve","SWEPT_FACE",FACE,{"disambiguationData":[OSD([sQuery(id+"F0.wireOp",EDGE,"E6")])]}),makeQuery(id+"F3.opExtrude","SWEPT_FACE",FACE,{"disambiguationData":[OSD([sQuery(id+"F2.wireOp",EDGE,"E26")])]})]});
            var Q93;
            Q93=makeQuery(id+"F3.boolean.opBoolean","INTERSECT",EDGE,{"derivedFrom":[makeQuery(id+"F1.opRevolve","SWEPT_FACE",FACE,{"disambiguationData":[OSD([sQuery(id+"F0.wireOp",EDGE,"E6")])]}),makeQuery(id+"F3.opExtrude","SWEPT_FACE",FACE,{"disambiguationData":[OSD([sQuery(id+"F2.wireOp",EDGE,"E41")])]})]});
            var Q94;
            Q94=makeQuery(id+"F3.boolean.opBoolean","INTERSECT",EDGE,{"derivedFrom":[makeQuery(id+"F1.opRevolve","SWEPT_FACE",FACE,{"disambiguationData":[OSD([sQuery(id+"F0.wireOp",EDGE,"E6")])]}),makeQuery(id+"F3.opExtrude","SWEPT_FACE",FACE,{"disambiguationData":[OSD([sQuery(id+"F2.wireOp",EDGE,"E25")])]})]});
            var Q95;
            Q95=makeQuery(id+"F3.boolean.opBoolean","INTERSECT",EDGE,{"derivedFrom":[makeQuery(id+"F1.opRevolve","SWEPT_FACE",FACE,{"disambiguationData":[OSD([sQuery(id+"F0.wireOp",EDGE,"E15")])]}),makeQuery(id+"F3.opExtrude","SWEPT_FACE",FACE,{"disambiguationData":[OSD([sQuery(id+"F2.wireOp",EDGE,"E24")])]})]});
            var Q96;
            Q96=makeQuery(id+"F3.boolean.opBoolean","INTERSECT",EDGE,{"derivedFrom":[makeQuery(id+"F1.opRevolve","SWEPT_FACE",FACE,{"disambiguationData":[OSD([sQuery(id+"F0.wireOp",EDGE,"E15")])]}),makeQuery(id+"F3.opExtrude","SWEPT_FACE",FACE,{"disambiguationData":[OSD([sQuery(id+"F2.wireOp",EDGE,"E23")])]})]});
            var Q97;
            Q97=makeQuery(id+"F3.boolean.opBoolean","INTERSECT",EDGE,{"derivedFrom":[makeQuery(id+"F1.opRevolve","SWEPT_FACE",FACE,{"disambiguationData":[OSD([sQuery(id+"F0.wireOp",EDGE,"E15")])]}),makeQuery(id+"F3.opExtrude","SWEPT_FACE",FACE,{"disambiguationData":[OSD([sQuery(id+"F2.wireOp",EDGE,"E27")])]})]});
            var Q98;
            Q98=makeQuery(id+"F3.opExtrude","SWEPT_EDGE",EDGE,{"disambiguationData":[OSD([sQuery(id+"F2.wireOp",EDGE,"E16.19"),sQuery(id+"F2.wireOp",EDGE,"E16.20"),sQuery(id+"F2.wireOp",EDGE,"E22"),sQuery(id+"F2.wireOp",EDGE,"E24")])]});
            var Q99;
            Q99=makeQuery(id+"F1.opRevolve","SWEPT_EDGE",EDGE,{"disambiguationData":[OSD([sQuery(id+"F0.wireOp",EDGE,"E8"),sQuery(id+"F0.wireOp",EDGE,"E9")])]});
            var Q100;
            Q100=makeQuery(id+"F3.opExtrude","SWEPT_EDGE",EDGE,{"disambiguationData":[OSD([sQuery(id+"F2.wireOp",EDGE,"E16.18"),sQuery(id+"F2.wireOp",EDGE,"E16.19"),sQuery(id+"F2.wireOp",EDGE,"E23"),sQuery(id+"F2.wireOp",EDGE,"E24")])]});
            var Q101;
            Q101=makeQuery(id+"F3.boolean.opBoolean","INTERSECT",EDGE,{"derivedFrom":[makeQuery(id+"F1.opRevolve","SWEPT_FACE",FACE,{"disambiguationData":[OSD([sQuery(id+"F0.wireOp",EDGE,"E15")])]}),makeQuery(id+"F3.opExtrude","SWEPT_FACE",FACE,{"disambiguationData":[OSD([sQuery(id+"F2.wireOp",EDGE,"E41")])]})]});
            var Q102;
            Q102=makeQuery(id+"F3.boolean.opBoolean","INTERSECT",EDGE,{"derivedFrom":[makeQuery(id+"F1.opRevolve","SWEPT_FACE",FACE,{"disambiguationData":[OSD([sQuery(id+"F0.wireOp",EDGE,"E6")])]}),makeQuery(id+"F3.opExtrude","SWEPT_FACE",FACE,{"disambiguationData":[OSD([sQuery(id+"F2.wireOp",EDGE,"E28")])]})]});
            var Q103;
            Q103=makeQuery(id+"F3.opExtrude","SWEPT_EDGE",EDGE,{"disambiguationData":[OSD([sQuery(id+"F2.wireOp",EDGE,"E16.22"),sQuery(id+"F2.wireOp",EDGE,"E16.23"),sQuery(id+"F2.wireOp",EDGE,"E19"),sQuery(id+"F2.wireOp",EDGE,"E20")])]});
            var Q104;
            Q104=makeQuery(id+"F3.boolean.opBoolean","INTERSECT",EDGE,{"derivedFrom":[makeQuery(id+"F1.opRevolve","SWEPT_FACE",FACE,{"disambiguationData":[OSD([sQuery(id+"F0.wireOp",EDGE,"E6")])]}),makeQuery(id+"F3.opExtrude","SWEPT_FACE",FACE,{"disambiguationData":[OSD([sQuery(id+"F2.wireOp",EDGE,"E19")])]})]});
            var Q105;
            Q105=makeQuery(id+"F3.opExtrude","SWEPT_EDGE",EDGE,{"disambiguationData":[OSD([sQuery(id+"F2.wireOp",EDGE,"E16.0"),sQuery(id+"F2.wireOp",EDGE,"E16.1"),sQuery(id+"F2.wireOp",EDGE,"E18"),sQuery(id+"F2.wireOp",EDGE,"E41")])]});
            var Q106;
            Q106=makeQuery(id+"F3.boolean.opBoolean","INTERSECT",EDGE,{"derivedFrom":[makeQuery(id+"F1.opRevolve","SWEPT_FACE",FACE,{"disambiguationData":[OSD([sQuery(id+"F0.wireOp",EDGE,"E6")])]}),makeQuery(id+"F3.opExtrude","SWEPT_FACE",FACE,{"disambiguationData":[OSD([sQuery(id+"F2.wireOp",EDGE,"E18")])]})]});
            var Q107;
            Q107=makeQuery(id+"F3.opExtrude","SWEPT_EDGE",EDGE,{"disambiguationData":[OSD([sQuery(id+"F2.wireOp",EDGE,"E16.12"),sQuery(id+"F2.wireOp",EDGE,"E16.13"),sQuery(id+"F2.wireOp",EDGE,"E29"),sQuery(id+"F2.wireOp",EDGE,"E30")])]});
            var Q108;
            Q108=makeQuery(id+"F3.boolean.opBoolean","INTERSECT",EDGE,{"derivedFrom":[makeQuery(id+"F1.opRevolve","SWEPT_FACE",FACE,{"disambiguationData":[OSD([sQuery(id+"F0.wireOp",EDGE,"E15")])]}),makeQuery(id+"F3.opExtrude","SWEPT_FACE",FACE,{"disambiguationData":[OSD([sQuery(id+"F2.wireOp",EDGE,"E29")])]})]});
            var Q109;
            Q109=makeQuery(id+"F3.boolean.opBoolean","INTERSECT",EDGE,{"derivedFrom":[makeQuery(id+"F1.opRevolve","SWEPT_FACE",FACE,{"disambiguationData":[OSD([sQuery(id+"F0.wireOp",EDGE,"E6")])]}),makeQuery(id+"F3.opExtrude","SWEPT_FACE",FACE,{"disambiguationData":[OSD([sQuery(id+"F2.wireOp",EDGE,"E29")])]})]});
            var Q110;
            Q110=makeQuery(id+"F3.boolean.opBoolean","INTERSECT",EDGE,{"derivedFrom":[makeQuery(id+"F1.opRevolve","SWEPT_FACE",FACE,{"disambiguationData":[OSD([sQuery(id+"F0.wireOp",EDGE,"E15")])]}),makeQuery(id+"F3.opExtrude","SWEPT_FACE",FACE,{"disambiguationData":[OSD([sQuery(id+"F2.wireOp",EDGE,"E18")])]})]});
            var Q111;
            Q111=makeQuery(id+"F3.opExtrude","SWEPT_EDGE",EDGE,{"disambiguationData":[OSD([sQuery(id+"F2.wireOp",EDGE,"E16.14"),sQuery(id+"F2.wireOp",EDGE,"E16.15"),sQuery(id+"F2.wireOp",EDGE,"E27"),sQuery(id+"F2.wireOp",EDGE,"E28")])]});
            var Q112;
            Q112=makeQuery(id+"F3.opExtrude","SWEPT_EDGE",EDGE,{"disambiguationData":[OSD([sQuery(id+"F2.wireOp",EDGE,"E16.13"),sQuery(id+"F2.wireOp",EDGE,"E16.14"),sQuery(id+"F2.wireOp",EDGE,"E28"),sQuery(id+"F2.wireOp",EDGE,"E29")])]});
            var Q113;
            Q113=makeQuery(id+"F3.opExtrude","SWEPT_EDGE",EDGE,{"disambiguationData":[OSD([sQuery(id+"F2.wireOp",EDGE,"E16.0"),sQuery(id+"F2.wireOp",EDGE,"E16.23"),sQuery(id+"F2.wireOp",EDGE,"E18"),sQuery(id+"F2.wireOp",EDGE,"E19")])]});
            fillet(context, id + "F4", {"entities" : qUnion([Q0, Q1, Q2, Q3, Q4, Q5, Q6, Q7, Q8, Q9, Q10, Q11, Q12, Q13, Q14, Q15, Q16, Q17, Q18, Q19, Q20, Q21, Q22, Q23, Q24, Q25, Q26, Q27, Q28, Q29, Q30, Q31, Q32, Q33, Q34, Q35, Q36, Q37, Q38, Q39, Q40, Q41, Q42, Q43, Q44, Q45, Q46, Q47, Q48, Q49, Q50, Q51, Q52, Q53, Q54, Q55, Q56, Q57, Q58, Q59, Q60, Q61, Q62, Q63, Q64, Q65, Q66, Q67, Q68, Q69, Q70, Q71, Q72, Q73, Q74, Q75, Q76, Q77, Q78, Q79, Q80, Q81, Q82, Q83, Q84, Q85, Q86, Q87, Q88, Q89, Q90, Q91, Q92, Q93, Q94, Q95, Q96, Q97, Q98, Q99, Q100, Q101, Q102, Q103, Q104, Q105, Q106, Q107, Q108, Q109, Q110, Q111, Q112, Q113]), "radius" : 5 * mm, "tangentPropagation" : true, "allowEdgeOverflow" : false});
        }
    });
